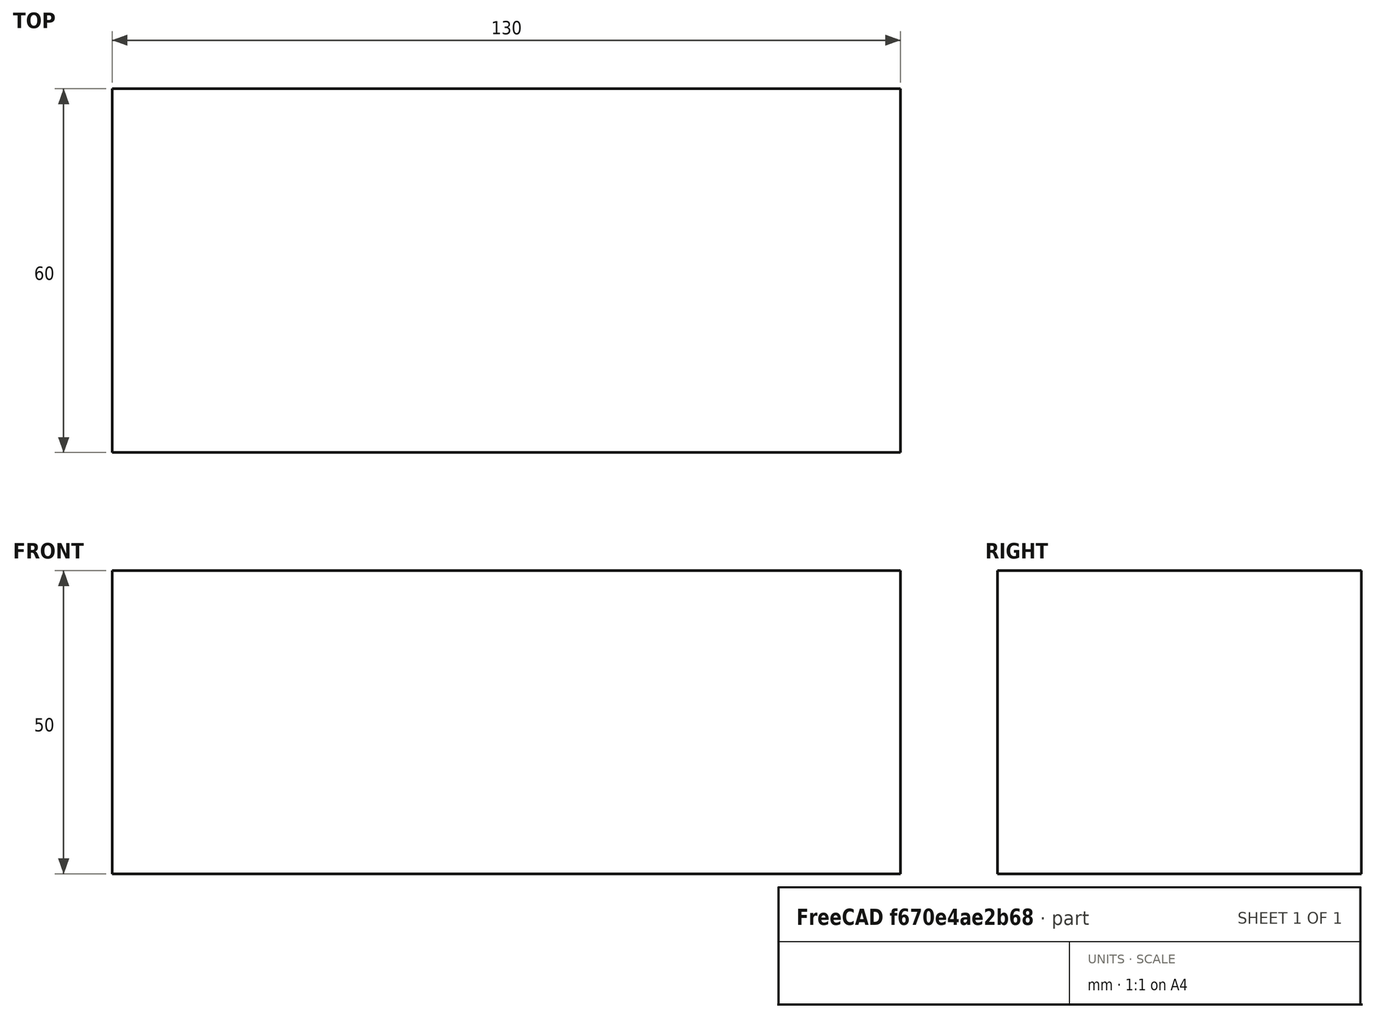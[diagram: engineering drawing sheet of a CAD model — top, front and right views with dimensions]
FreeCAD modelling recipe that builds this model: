
FCSTD DOCUMENT  (FreeCAD 0.15R4671 (Git))
Label: Flat Bar 130x60 EN10058 S235JR
License: All rights reserved
LicenseURL: http://en.wikipedia.org/wiki/All_rights_reserved
objects: Sketcher::SketchObject×1, Part::Extrusion×1
note: 2 computed .brp shape members not serialized (recipe doc carries the construction recipe); baked Part::Feature solids carry a one-line shape summary decoded from their .brp

FEATURE [Sketcher::SketchObject] Sketch
  sketch-geometry (4):
    g0: LineSegment StartX=-65 StartY=-30 StartZ=0 EndX=65 EndY=-30 EndZ=0
    g1: LineSegment StartX=65 StartY=-30 StartZ=0 EndX=65 EndY=30 EndZ=0
    g2: LineSegment StartX=65 StartY=30 StartZ=0 EndX=-65 EndY=30 EndZ=0
    g3: LineSegment StartX=-65 StartY=30 StartZ=0 EndX=-65 EndY=-30 EndZ=0
  constraints (12):
    c: Coincident(g0,g1)
    c: Coincident(g1,g2)
    c: Coincident(g2,g3)
    c: Coincident(g3,g0)
    c: Horizontal(g0)
    c: Horizontal(g2)
    c: Vertical(g1)
    c: Vertical(g3)
    c: Symmetric(g1,g2,g-2)
    c: Symmetric(g0,g1,g-1)
    c: DistanceY(g1) = 60
    c: DistanceX(g0) = 130
FEATURE [Part::Extrusion] Extrude  label="Flat Bar 130x60 EN10058 S235JR"
  Base = -> Sketch
  Dir = (0,0,50)
  Solid = true
